# Revit family: Casement_38_I_Top_Hung_Standard
name_source: partatom
category: Windows
revit_build: Autodesk Revit 2014 (Build: 20130308_1515(x64)
units: mm (PartAtom-declared; Revit-internal decimal feet)

## types (24) — shared parameters
Aluminium Thickness = 1 mm  [stored 0.00328084 ft]
Bead SG Gap = 13 mm  [stored 0.0426509 ft]
Bottom Hung = No
Casement Dimension = 38 mm  [stored 0.124672 ft]
Custom Sash Bottom Height = 554 mm  [stored 1.81759 ft]
Custom Sash Top Height = 554 mm  [stored 1.81759 ft]
DG Extrusion Start = 9 mm  [stored 0.0295276 ft]
DG Gasket Finish = Double Glazing Gasket Material
Default Sill Height = 800 mm  [stored 2.62467 ft]
Depth Bead = 24 mm  [stored 0.0787402 ft]
Description = Window 38mm, Type I top hung
Frame Center Offset = 19 mm  [stored 0.062336 ft]
Height Panel 1 = 540 mm  [stored 1.77165 ft]
Height Panel 2 = 540 mm  [stored 1.77165 ft]
Height Sash Bottom = 524 mm  [stored 1.71916 ft]
Height Sash Bottom Opening = 554 mm  [stored 1.81759 ft]
Height Sash Top = 524 mm  [stored 1.71916 ft]
Height Sash Top Opening = 554 mm  [stored 1.81759 ft]
Limit Fixed Pane Height Max = 1800 mm
Limit Fixed Pane Height Min = 200 mm  [stored 0.656168 ft]
Limit Fixed Pane Width Max = 1500 mm
Limit Fixed Pane Width Min = 200 mm  [stored 0.656168 ft]
Limit Sash Bottom Height Min = 300 mm  [stored 0.984252 ft]
Limit Sash Top Height Max = 1200 mm
Limit Sash Top Height Min = 300 mm  [stored 0.984252 ft]
Limit Sash Width Max = 1500 mm
Limit Sash Width Min = 300 mm  [stored 0.984252 ft]
Limit Window Height Max = 1860 mm
Limit Window Height Min = 1400 mm
Manufacturer = Crealco
Max System DG One Piece Thickness = 6 mm  [stored 0.019685 ft]
Max System DG Unit Thickness = 25 mm  [stored 0.082021 ft]
Model = Casement 38
Offset Bead SG Center Reversed = 19 mm  [stored 0.062336 ft]
Offset Panel 3 Bead Top = 1170 mm
Offset Sash 1 Top = 23 mm  [stored 0.0754593 ft]
Offset Sash 2 Top = 593 mm  [stored 1.94554 ft]
Offset Sash Left = 23 mm  [stored 0.0754593 ft]
Offset Transom 1 Top = 570 mm  [stored 1.87008 ft]
Offset Transom 2 Top = 1140 mm
Offset Window Exterior = 19 mm  [stored 0.062336 ft]
SG Gasket Thickness = 6 mm  [stored 0.019685 ft]
Sash Center Offset = 16 mm  [stored 0.0524934 ft]
Sash Overlap = 7 mm  [stored 0.0229659 ft]
Sash Spacing Inner = 8 mm  [stored 0.0262467 ft]
Top Hung = Yes
URL = http://www.crealco.co.za
Wall Closure = By host
Width Bead = 15 mm  [stored 0.0492126 ft]
Width Profile = 30 mm  [stored 0.0984252 ft]
zero-valued in all types: Window Exterior Offset

## per-type parameters (varying)
- 38-1215DT-1000Pa: Area Pane Left Bottom=0.15 m²; Area Pane Left Middle=0.23 m²; Area Pane Left Top=0.23 m²; Area Pane Right=0.78 m²; Clearvue Insulated LowE SHGC Value=0.709; Clearvue Insulated LowE U Value=5; Clearvue Insulated SHGC Value=0.778; Clearvue Insulated U Value=5.75; Clearvue SHGC Value=0.987; Clearvue U Value=8.9; Custom Sash Width=554 mm  [stored 1.81759 ft]; Custom Windload=1000 mm; Custom Window Height=1490 mm; Custom Window Width=1190 mm; DG Thickness Calc=4 mm  [stored 0.0131234 ft]; Depth Mullion=39 mm  [stored 0.127953 ft]; Energy Advantage SHGC Value=0.804; Energy Advantage U Value=6.7; Height=1490 mm; Height Panel 3=290 mm  [stored 0.951444 ft]; Height Panel 4=1430 mm; Intruderprufe Insulated LowE SHGC Value=0.658; Intruderprufe Insulated LowE U Value=4.9; Intruderprufe Insulated SHGC Value=0.722; Intruderprufe Insulated U Value=5.61; Intruderprufe LowE SHGC Value=0.747; Intruderprufe LowE U Value=6.54; Intruderprufe SHGC Value=0.872; Intruderprufe U Value=8.8; Length Mullion=1490 mm; Length Transom=540 mm  [stored 1.77165 ft]; Limit Sash Bottom Height Max=644 mm  [stored 2.11286 ft]; Limit Sash Bottom Height Max Based On Top Sash=644 mm  [stored 2.11286 ft]; Limit Sash Bottom Height Max Calc=644 mm  [stored 2.11286 ft]; Limit Window Width Max=2130 mm; Limit Window Width Min=830 mm  [stored 2.7231 ft]; Max Pane Area=0.78 m²; Mullion Depth Windload Based=39 mm  [stored 0.127953 ft]; Offset Mullion Left=570 mm  [stored 1.87008 ft]; Offset Panel 4 Left=600 mm  [stored 1.9685 ft]; Width=1190 mm; Width Panel 1=540 mm  [stored 1.77165 ft]; Width Panel 2=540 mm  [stored 1.77165 ft]; Width Panel 3=540 mm  [stored 1.77165 ft]; Width Panel 4=560 mm  [stored 1.83727 ft]; Width Sash 1=524 mm  [stored 1.71916 ft]; Width Sash 2=524 mm  [stored 1.71916 ft]; Width Sash Opening=554 mm  [stored 1.81759 ft]; Windload Design=1000 mm
- 38-1215DT-1500Pa: Area Pane Left Bottom=0.15 m²; Area Pane Left Middle=0.23 m²; Area Pane Left Top=0.23 m²; Area Pane Right=0.78 m²; Clearvue Insulated LowE SHGC Value=0.709; Clearvue Insulated LowE U Value=5.06; Clearvue Insulated SHGC Value=0.779; Clearvue Insulated U Value=5.81; Clearvue SHGC Value=0.896; Clearvue U Value=8.9; Custom Sash Width=554 mm  [stored 1.81759 ft]; Custom Windload=1500 mm; Custom Window Height=1490 mm; Custom Window Width=1190 mm; DG Thickness Calc=4 mm  [stored 0.0131234 ft]; Depth Mullion=54 mm  [stored 0.177165 ft]; Energy Advantage SHGC Value=0.803; Energy Advantage U Value=6.77; Height=1490 mm; Height Panel 3=290 mm  [stored 0.951444 ft]; Height Panel 4=1430 mm; Intruderprufe Insulated LowE SHGC Value=0.66; Intruderprufe Insulated LowE U Value=4.95; Intruderprufe Insulated SHGC Value=0.724; Intruderprufe Insulated U Value=5.67; Intruderprufe LowE SHGC Value=0.749; Intruderprufe LowE U Value=6.61; Intruderprufe SHGC Value=0.859; Intruderprufe U Value=8.82; Length Mullion=1490 mm; Length Transom=540 mm  [stored 1.77165 ft]; Limit Sash Bottom Height Max=644 mm  [stored 2.11286 ft]; Limit Sash Bottom Height Max Based On Top Sash=644 mm  [stored 2.11286 ft]; Limit Sash Bottom Height Max Calc=644 mm  [stored 2.11286 ft]; Limit Window Width Max=2130 mm; Limit Window Width Min=830 mm  [stored 2.7231 ft]; Max Pane Area=0.78 m²; Mullion Depth Windload Based=54 mm  [stored 0.177165 ft]; Offset Mullion Left=570 mm  [stored 1.87008 ft]; Offset Panel 4 Left=600 mm  [stored 1.9685 ft]; Width=1190 mm; Width Panel 1=540 mm  [stored 1.77165 ft]; Width Panel 2=540 mm  [stored 1.77165 ft]; Width Panel 3=540 mm  [stored 1.77165 ft]; Width Panel 4=560 mm  [stored 1.83727 ft]; Width Sash 1=524 mm  [stored 1.71916 ft]; Width Sash 2=524 mm  [stored 1.71916 ft]; Width Sash Opening=554 mm  [stored 1.81759 ft]; Windload Design=1500 mm
- 38-1215DT-2000Pa: Area Pane Left Bottom=0.15 m²; Area Pane Left Middle=0.23 m²; Area Pane Left Top=0.23 m²; Area Pane Right=0.78 m²; Clearvue Insulated LowE SHGC Value=0.709; Clearvue Insulated LowE U Value=5.06; Clearvue Insulated SHGC Value=0.779; Clearvue Insulated U Value=5.81; Clearvue SHGC Value=0.896; Clearvue U Value=8.9; Custom Sash Width=554 mm  [stored 1.81759 ft]; Custom Windload=2000 mm; Custom Window Height=1490 mm; Custom Window Width=1190 mm; DG Thickness Calc=4 mm  [stored 0.0131234 ft]; Depth Mullion=54 mm  [stored 0.177165 ft]; Energy Advantage SHGC Value=0.803; Energy Advantage U Value=6.77; Height=1490 mm; Height Panel 3=290 mm  [stored 0.951444 ft]; Height Panel 4=1430 mm; Intruderprufe Insulated LowE SHGC Value=0.66; Intruderprufe Insulated LowE U Value=4.95; Intruderprufe Insulated SHGC Value=0.724; Intruderprufe Insulated U Value=5.67; Intruderprufe LowE SHGC Value=0.749; Intruderprufe LowE U Value=6.61; Intruderprufe SHGC Value=0.859; Intruderprufe U Value=8.82; Length Mullion=1490 mm; Length Transom=540 mm  [stored 1.77165 ft]; Limit Sash Bottom Height Max=644 mm  [stored 2.11286 ft]; Limit Sash Bottom Height Max Based On Top Sash=644 mm  [stored 2.11286 ft]; Limit Sash Bottom Height Max Calc=644 mm  [stored 2.11286 ft]; Limit Window Width Max=2130 mm; Limit Window Width Min=830 mm  [stored 2.7231 ft]; Max Pane Area=0.78 m²; Mullion Depth Windload Based=54 mm  [stored 0.177165 ft]; Offset Mullion Left=570 mm  [stored 1.87008 ft]; Offset Panel 4 Left=600 mm  [stored 1.9685 ft]; Width=1190 mm; Width Panel 1=540 mm  [stored 1.77165 ft]; Width Panel 2=540 mm  [stored 1.77165 ft]; Width Panel 3=540 mm  [stored 1.77165 ft]; Width Panel 4=560 mm  [stored 1.83727 ft]; Width Sash 1=524 mm  [stored 1.71916 ft]; Width Sash 2=524 mm  [stored 1.71916 ft]; Width Sash Opening=554 mm  [stored 1.81759 ft]; Windload Design=2000 mm
- 38-1515DT-1000Pa: Area Pane Left Bottom=0.15 m²; Area Pane Left Middle=0.23 m²; Area Pane Left Top=0.23 m²; Area Pane Right=1.21 m²; Clearvue Insulated LowE SHGC Value=0.822; Clearvue Insulated LowE U Value=5.14; Clearvue Insulated SHGC Value=0.904; Clearvue Insulated U Value=6.03; Clearvue SHGC Value=1.037; Clearvue U Value=9.66; Custom Sash Width=554 mm  [stored 1.81759 ft]; Custom Windload=1000 mm; Custom Window Height=1490 mm; Custom Window Width=1490 mm; DG Thickness Calc=4 mm  [stored 0.0131234 ft]; Depth Mullion=54 mm  [stored 0.177165 ft]; Energy Advantage SHGC Value=0.928; Energy Advantage U Value=7.19; Height=1490 mm; Height Panel 3=290 mm  [stored 0.951444 ft]; Height Panel 4=1430 mm; Intruderprufe Insulated LowE SHGC Value=0.763; Intruderprufe Insulated LowE U Value=5.04; Intruderprufe Insulated SHGC Value=0.839; Intruderprufe Insulated U Value=5.89; Intruderprufe LowE SHGC Value=0.865; Intruderprufe LowE U Value=6.99; Intruderprufe SHGC Value=0.989; Intruderprufe U Value=9.55; Length Mullion=1490 mm; Length Transom=540 mm  [stored 1.77165 ft]; Limit Sash Bottom Height Max=644 mm  [stored 2.11286 ft]; Limit Sash Bottom Height Max Based On Top Sash=644 mm  [stored 2.11286 ft]; Limit Sash Bottom Height Max Calc=644 mm  [stored 2.11286 ft]; Limit Window Width Max=2130 mm; Limit Window Width Min=830 mm  [stored 2.7231 ft]; Max Pane Area=1.21 m²; Mullion Depth Windload Based=54 mm  [stored 0.177165 ft]; Offset Mullion Left=570 mm  [stored 1.87008 ft]; Offset Panel 4 Left=600 mm  [stored 1.9685 ft]; Width=1490 mm; Width Panel 1=540 mm  [stored 1.77165 ft]; Width Panel 2=540 mm  [stored 1.77165 ft]; Width Panel 3=540 mm  [stored 1.77165 ft]; Width Panel 4=860 mm  [stored 2.82152 ft]; Width Sash 1=524 mm  [stored 1.71916 ft]; Width Sash 2=524 mm  [stored 1.71916 ft]; Width Sash Opening=554 mm  [stored 1.81759 ft]; Windload Design=1000 mm
- 38-1515DT-1500Pa: Area Pane Left Bottom=0.15 m²; Area Pane Left Middle=0.23 m²; Area Pane Left Top=0.23 m²; Area Pane Right=1.21 m²; Clearvue Insulated LowE SHGC Value=0.822; Clearvue Insulated LowE U Value=5.14; Clearvue Insulated SHGC Value=0.904; Clearvue Insulated U Value=6.03; Clearvue SHGC Value=1.037; Clearvue U Value=9.66; Custom Sash Width=554 mm  [stored 1.81759 ft]; Custom Windload=1500 mm; Custom Window Height=1490 mm; Custom Window Width=1490 mm; DG Thickness Calc=4 mm  [stored 0.0131234 ft]; Depth Mullion=54 mm  [stored 0.177165 ft]; Energy Advantage SHGC Value=0.928; Energy Advantage U Value=7.19; Height=1490 mm; Height Panel 3=290 mm  [stored 0.951444 ft]; Height Panel 4=1430 mm; Intruderprufe Insulated LowE SHGC Value=0.763; Intruderprufe Insulated LowE U Value=5.04; Intruderprufe Insulated SHGC Value=0.839; Intruderprufe Insulated U Value=5.89; Intruderprufe LowE SHGC Value=0.865; Intruderprufe LowE U Value=6.99; Intruderprufe SHGC Value=0.989; Intruderprufe U Value=9.55; Length Mullion=1490 mm; Length Transom=540 mm  [stored 1.77165 ft]; Limit Sash Bottom Height Max=644 mm  [stored 2.11286 ft]; Limit Sash Bottom Height Max Based On Top Sash=644 mm  [stored 2.11286 ft]; Limit Sash Bottom Height Max Calc=644 mm  [stored 2.11286 ft]; Limit Window Width Max=2130 mm; Limit Window Width Min=830 mm  [stored 2.7231 ft]; Max Pane Area=1.21 m²; Mullion Depth Windload Based=54 mm  [stored 0.177165 ft]; Offset Mullion Left=570 mm  [stored 1.87008 ft]; Offset Panel 4 Left=600 mm  [stored 1.9685 ft]; Width=1490 mm; Width Panel 1=540 mm  [stored 1.77165 ft]; Width Panel 2=540 mm  [stored 1.77165 ft]; Width Panel 3=540 mm  [stored 1.77165 ft]; Width Panel 4=860 mm  [stored 2.82152 ft]; Width Sash 1=524 mm  [stored 1.71916 ft]; Width Sash 2=524 mm  [stored 1.71916 ft]; Width Sash Opening=554 mm  [stored 1.81759 ft]; Windload Design=1500 mm
- 38-1515DT-2000Pa: Area Pane Left Bottom=0.15 m²; Area Pane Left Middle=0.23 m²; Area Pane Left Top=0.23 m²; Area Pane Right=1.21 m²; Clearvue Insulated LowE SHGC Value=0.822; Clearvue Insulated LowE U Value=5.14; Clearvue Insulated SHGC Value=0.904; Clearvue Insulated U Value=6.03; Clearvue SHGC Value=1.037; Clearvue U Value=9.66; Custom Sash Width=554 mm  [stored 1.81759 ft]; Custom Windload=2000 mm; Custom Window Height=1490 mm; Custom Window Width=1490 mm; DG Thickness Calc=4 mm  [stored 0.0131234 ft]; Depth Mullion=54 mm  [stored 0.177165 ft]; Energy Advantage SHGC Value=0.928; Energy Advantage U Value=7.19; Height=1490 mm; Height Panel 3=290 mm  [stored 0.951444 ft]; Height Panel 4=1430 mm; Intruderprufe Insulated LowE SHGC Value=0.763; Intruderprufe Insulated LowE U Value=5.04; Intruderprufe Insulated SHGC Value=0.839; Intruderprufe Insulated U Value=5.89; Intruderprufe LowE SHGC Value=0.865; Intruderprufe LowE U Value=6.99; Intruderprufe SHGC Value=0.989; Intruderprufe U Value=9.55; Length Mullion=1490 mm; Length Transom=540 mm  [stored 1.77165 ft]; Limit Sash Bottom Height Max=644 mm  [stored 2.11286 ft]; Limit Sash Bottom Height Max Based On Top Sash=644 mm  [stored 2.11286 ft]; Limit Sash Bottom Height Max Calc=644 mm  [stored 2.11286 ft]; Limit Window Width Max=2130 mm; Limit Window Width Min=830 mm  [stored 2.7231 ft]; Max Pane Area=1.21 m²; Mullion Depth Windload Based=54 mm  [stored 0.177165 ft]; Offset Mullion Left=570 mm  [stored 1.87008 ft]; Offset Panel 4 Left=600 mm  [stored 1.9685 ft]; Width=1490 mm; Width Panel 1=540 mm  [stored 1.77165 ft]; Width Panel 2=540 mm  [stored 1.77165 ft]; Width Panel 3=540 mm  [stored 1.77165 ft]; Width Panel 4=860 mm  [stored 2.82152 ft]; Width Sash 1=524 mm  [stored 1.71916 ft]; Width Sash 2=524 mm  [stored 1.71916 ft]; Width Sash Opening=554 mm  [stored 1.81759 ft]; Windload Design=2000 mm
- 38-1815DT-1000Pa: Area Pane Left Bottom=0.23 m²; Area Pane Left Middle=0.38 m²; Area Pane Left Top=0.38 m²; Area Pane Right=1.21 m²; Clearvue Insulated LowE SHGC Value=0.755; Clearvue Insulated LowE U Value=4.65; Clearvue Insulated SHGC Value=0.83; Clearvue Insulated U Value=5.47; Clearvue SHGC Value=0.955; Clearvue U Value=8.8; Custom Sash Width=854 mm  [stored 2.80184 ft]; Custom Windload=1000 mm; Custom Window Height=1490 mm; Custom Window Width=1790 mm; DG Thickness Calc=4 mm  [stored 0.0131234 ft]; Depth Mullion=54 mm  [stored 0.177165 ft]; Energy Advantage SHGC Value=0.854; Energy Advantage U Value=6.5; Height=1490 mm; Height Panel 3=290 mm  [stored 0.951444 ft]; Height Panel 4=1430 mm; Intruderprufe Insulated LowE SHGC Value=0.7; Intruderprufe Insulated LowE U Value=4.56; Intruderprufe Insulated SHGC Value=0.77; Intruderprufe Insulated U Value=5.34; Intruderprufe LowE SHGC Value=0.794; Intruderprufe LowE U Value=6.35; Intruderprufe SHGC Value=0.914; Intruderprufe U Value=8.73; Length Mullion=1490 mm; Length Transom=840 mm; Limit Sash Bottom Height Max=644 mm  [stored 2.11286 ft]; Limit Sash Bottom Height Max Based On Top Sash=644 mm  [stored 2.11286 ft]; Limit Sash Bottom Height Max Calc=644 mm  [stored 2.11286 ft]; Limit Window Width Max=2430 mm; Limit Window Width Min=1130 mm; Max Pane Area=1.21 m²; Mullion Depth Windload Based=54 mm  [stored 0.177165 ft]; Offset Mullion Left=870 mm  [stored 2.85433 ft]; Offset Panel 4 Left=900 mm  [stored 2.95276 ft]; Width=1790 mm; Width Panel 1=840 mm; Width Panel 2=840 mm; Width Panel 3=840 mm; Width Panel 4=860 mm  [stored 2.82152 ft]; Width Sash 1=824 mm; Width Sash 2=824 mm; Width Sash Opening=854 mm  [stored 2.80184 ft]; Windload Design=1000 mm
- 38-1815DT-1500Pa: Area Pane Left Bottom=0.23 m²; Area Pane Left Middle=0.38 m²; Area Pane Left Top=0.38 m²; Area Pane Right=1.21 m²; Clearvue Insulated LowE SHGC Value=0.755; Clearvue Insulated LowE U Value=4.65; Clearvue Insulated SHGC Value=0.83; Clearvue Insulated U Value=5.47; Clearvue SHGC Value=0.955; Clearvue U Value=8.8; Custom Sash Width=854 mm  [stored 2.80184 ft]; Custom Windload=1500 mm; Custom Window Height=1490 mm; Custom Window Width=1790 mm; DG Thickness Calc=4 mm  [stored 0.0131234 ft]; Depth Mullion=54 mm  [stored 0.177165 ft]; Energy Advantage SHGC Value=0.854; Energy Advantage U Value=6.5; Height=1490 mm; Height Panel 3=290 mm  [stored 0.951444 ft]; Height Panel 4=1430 mm; Intruderprufe Insulated LowE SHGC Value=0.7; Intruderprufe Insulated LowE U Value=4.56; Intruderprufe Insulated SHGC Value=0.77; Intruderprufe Insulated U Value=5.34; Intruderprufe LowE SHGC Value=0.794; Intruderprufe LowE U Value=6.35; Intruderprufe SHGC Value=0.914; Intruderprufe U Value=8.73; Length Mullion=1490 mm; Length Transom=840 mm; Limit Sash Bottom Height Max=644 mm  [stored 2.11286 ft]; Limit Sash Bottom Height Max Based On Top Sash=644 mm  [stored 2.11286 ft]; Limit Sash Bottom Height Max Calc=644 mm  [stored 2.11286 ft]; Limit Window Width Max=2430 mm; Limit Window Width Min=1130 mm; Max Pane Area=1.21 m²; Mullion Depth Windload Based=54 mm  [stored 0.177165 ft]; Offset Mullion Left=870 mm  [stored 2.85433 ft]; Offset Panel 4 Left=900 mm  [stored 2.95276 ft]; Width=1790 mm; Width Panel 1=840 mm; Width Panel 2=840 mm; Width Panel 3=840 mm; Width Panel 4=860 mm  [stored 2.82152 ft]; Width Sash 1=824 mm; Width Sash 2=824 mm; Width Sash Opening=854 mm  [stored 2.80184 ft]; Windload Design=1500 mm
- 38-1815DT-2000Pa: Area Pane Left Bottom=0.23 m²; Area Pane Left Middle=0.38 m²; Area Pane Left Top=0.38 m²; Area Pane Right=1.21 m²; Clearvue Insulated LowE SHGC Value=0.756; Clearvue Insulated LowE U Value=4.72; Clearvue Insulated SHGC Value=0.831; Clearvue Insulated U Value=5.53; Clearvue SHGC Value=0.955; Clearvue U Value=8.75; Custom Sash Width=854 mm  [stored 2.80184 ft]; Custom Windload=2000 mm; Custom Window Height=1490 mm; Custom Window Width=1790 mm; DG Thickness Calc=4 mm  [stored 0.0131234 ft]; Depth Mullion=70 mm  [stored 0.229659 ft]; Energy Advantage SHGC Value=0.856; Energy Advantage U Value=6.58; Height=1490 mm; Height Panel 3=290 mm  [stored 0.951444 ft]; Height Panel 4=1430 mm; Intruderprufe Insulated LowE SHGC Value=0.7; Intruderprufe Insulated LowE U Value=4.62; Intruderprufe Insulated SHGC Value=0.77; Intruderprufe Insulated U Value=5.4; Intruderprufe LowE SHGC Value=0.794; Intruderprufe LowE U Value=6.43; Intruderprufe SHGC Value=0.906; Intruderprufe U Value=8.74; Length Mullion=1490 mm; Length Transom=840 mm; Limit Sash Bottom Height Max=644 mm  [stored 2.11286 ft]; Limit Sash Bottom Height Max Based On Top Sash=644 mm  [stored 2.11286 ft]; Limit Sash Bottom Height Max Calc=644 mm  [stored 2.11286 ft]; Limit Window Width Max=2430 mm; Limit Window Width Min=1130 mm; Max Pane Area=1.21 m²; Mullion Depth Windload Based=70 mm  [stored 0.229659 ft]; Offset Mullion Left=870 mm  [stored 2.85433 ft]; Offset Panel 4 Left=900 mm  [stored 2.95276 ft]; Width=1790 mm; Width Panel 1=840 mm; Width Panel 2=840 mm; Width Panel 3=840 mm; Width Panel 4=860 mm  [stored 2.82152 ft]; Width Sash 1=824 mm; Width Sash 2=824 mm; Width Sash Opening=854 mm  [stored 2.80184 ft]; Windload Design=2000 mm
- 38-2415DT-1000Pa: Area Pane Left Bottom=0.23 m²; Area Pane Left Middle=0.38 m²; Area Pane Left Top=0.38 m²; Area Pane Right=2.06 m²; Clearvue Insulated LowE SHGC Value=0.892; Clearvue Insulated LowE U Value=4.82; Clearvue Insulated SHGC Value=0.981; Clearvue Insulated U Value=5.81; Clearvue SHGC Value=0; Clearvue U Value=7.9; Custom Sash Width=854 mm  [stored 2.80184 ft]; Custom Windload=1000 mm; Custom Window Height=1490 mm; Custom Window Width=2390 mm; DG Thickness Calc=4 mm  [stored 0.0131234 ft]; Depth Mullion=54 mm  [stored 0.177165 ft]; Energy Advantage SHGC Value=0; Energy Advantage U Value=7.9; Height=1490 mm; Height Panel 3=290 mm  [stored 0.951444 ft]; Height Panel 4=1430 mm; Intruderprufe Insulated LowE SHGC Value=0.825; Intruderprufe Insulated LowE U Value=4.73; Intruderprufe Insulated SHGC Value=0.909; Intruderprufe Insulated U Value=5.68; Intruderprufe LowE SHGC Value=0.936; Intruderprufe LowE U Value=6.88; Intruderprufe SHGC Value=1.072; Intruderprufe U Value=9.68; Length Mullion=1490 mm; Length Transom=840 mm; Limit Sash Bottom Height Max=644 mm  [stored 2.11286 ft]; Limit Sash Bottom Height Max Based On Top Sash=644 mm  [stored 2.11286 ft]; Limit Sash Bottom Height Max Calc=644 mm  [stored 2.11286 ft]; Limit Window Width Max=2430 mm; Limit Window Width Min=1130 mm; Max Pane Area=2.06 m²; Mullion Depth Windload Based=54 mm  [stored 0.177165 ft]; Offset Mullion Left=870 mm  [stored 2.85433 ft]; Offset Panel 4 Left=900 mm  [stored 2.95276 ft]; Width=2390 mm; Width Panel 1=840 mm; Width Panel 2=840 mm; Width Panel 3=840 mm; Width Panel 4=1460 mm; Width Sash 1=824 mm; Width Sash 2=824 mm; Width Sash Opening=854 mm  [stored 2.80184 ft]; Windload Design=1000 mm
- 38-2415DT-1500Pa: Area Pane Left Bottom=0.23 m²; Area Pane Left Middle=0.38 m²; Area Pane Left Top=0.38 m²; Area Pane Right=2.06 m²; Clearvue Insulated LowE SHGC Value=0.893; Clearvue Insulated LowE U Value=4.88; Clearvue Insulated SHGC Value=0.982; Clearvue Insulated U Value=5.86; Clearvue SHGC Value=0; Clearvue U Value=7.9; Custom Sash Width=854 mm  [stored 2.80184 ft]; Custom Windload=1500 mm; Custom Window Height=1490 mm; Custom Window Width=2390 mm; DG Thickness Calc=4 mm  [stored 0.0131234 ft]; Depth Mullion=54 mm  [stored 0.177165 ft]; Energy Advantage SHGC Value=0; Energy Advantage U Value=7.9; Height=1490 mm; Height Panel 3=290 mm  [stored 0.951444 ft]; Height Panel 4=1430 mm; Intruderprufe Insulated LowE SHGC Value=0.825; Intruderprufe Insulated LowE U Value=4.78; Intruderprufe Insulated SHGC Value=0.91; Intruderprufe Insulated U Value=5.73; Intruderprufe LowE SHGC Value=0.936; Intruderprufe LowE U Value=6.95; Intruderprufe SHGC Value=1.065; Intruderprufe U Value=9.69; Length Mullion=1490 mm; Length Transom=840 mm; Limit Sash Bottom Height Max=644 mm  [stored 2.11286 ft]; Limit Sash Bottom Height Max Based On Top Sash=644 mm  [stored 2.11286 ft]; Limit Sash Bottom Height Max Calc=644 mm  [stored 2.11286 ft]; Limit Window Width Max=2430 mm; Limit Window Width Min=1130 mm; Max Pane Area=2.06 m²; Mullion Depth Windload Based=54 mm  [stored 0.177165 ft]; Offset Mullion Left=870 mm  [stored 2.85433 ft]; Offset Panel 4 Left=900 mm  [stored 2.95276 ft]; Width=2390 mm; Width Panel 1=840 mm; Width Panel 2=840 mm; Width Panel 3=840 mm; Width Panel 4=1460 mm; Width Sash 1=824 mm; Width Sash 2=824 mm; Width Sash Opening=854 mm  [stored 2.80184 ft]; Windload Design=1500 mm
- 38-2415DT-2000Pa: Area Pane Left Bottom=0.23 m²; Area Pane Left Middle=0.38 m²; Area Pane Left Top=0.38 m²; Area Pane Right=2.06 m²; Clearvue Insulated LowE SHGC Value=0.893; Clearvue Insulated LowE U Value=4.88; Clearvue Insulated SHGC Value=0.982; Clearvue Insulated U Value=5.86; Clearvue SHGC Value=0; Clearvue U Value=7.9; Custom Sash Width=854 mm  [stored 2.80184 ft]; Custom Windload=2000 mm; Custom Window Height=1490 mm; Custom Window Width=2390 mm; DG Thickness Calc=4 mm  [stored 0.0131234 ft]; Depth Mullion=70 mm  [stored 0.229659 ft]; Energy Advantage SHGC Value=0; Energy Advantage U Value=7.9; Height=1490 mm; Height Panel 3=290 mm  [stored 0.951444 ft]; Height Panel 4=1430 mm; Intruderprufe Insulated LowE SHGC Value=0.825; Intruderprufe Insulated LowE U Value=4.78; Intruderprufe Insulated SHGC Value=0.91; Intruderprufe Insulated U Value=5.73; Intruderprufe LowE SHGC Value=0.936; Intruderprufe LowE U Value=6.95; Intruderprufe SHGC Value=1.065; Intruderprufe U Value=9.69; Length Mullion=1490 mm; Length Transom=840 mm; Limit Sash Bottom Height Max=644 mm  [stored 2.11286 ft]; Limit Sash Bottom Height Max Based On Top Sash=644 mm  [stored 2.11286 ft]; Limit Sash Bottom Height Max Calc=644 mm  [stored 2.11286 ft]; Limit Window Width Max=2430 mm; Limit Window Width Min=1130 mm; Max Pane Area=2.06 m²; Mullion Depth Windload Based=70 mm  [stored 0.229659 ft]; Offset Mullion Left=870 mm  [stored 2.85433 ft]; Offset Panel 4 Left=900 mm  [stored 2.95276 ft]; Width=2390 mm; Width Panel 1=840 mm; Width Panel 2=840 mm; Width Panel 3=840 mm; Width Panel 4=1460 mm; Width Sash 1=824 mm; Width Sash 2=824 mm; Width Sash Opening=854 mm  [stored 2.80184 ft]; Windload Design=2000 mm
- 38-1218DT-1000Pa: Area Pane Left Bottom=0.31 m²; Area Pane Left Middle=0.23 m²; Area Pane Left Top=0.23 m²; Area Pane Right=0.95 m²; Clearvue Insulated LowE SHGC Value=0.767; Clearvue Insulated LowE U Value=5.14; Clearvue Insulated SHGC Value=0.842; Clearvue Insulated U Value=5.95; Clearvue SHGC Value=0.967; Clearvue U Value=9.31; Custom Sash Width=554 mm  [stored 1.81759 ft]; Custom Windload=1000 mm; Custom Window Height=1790 mm; Custom Window Width=1190 mm; DG Thickness Calc=4 mm  [stored 0.0131234 ft]; Depth Mullion=54 mm  [stored 0.177165 ft]; Energy Advantage SHGC Value=0.899; Energy Advantage U Value=6.99; Height=1790 mm; Height Panel 3=590 mm; Height Panel 4=1730 mm; Intruderprufe Insulated LowE SHGC Value=0.712; Intruderprufe Insulated LowE U Value=5.03; Intruderprufe Insulated SHGC Value=0.783; Intruderprufe Insulated U Value=5.81; Intruderprufe LowE SHGC Value=0.808; Intruderprufe LowE U Value=6.84; Intruderprufe SHGC Value=0.924; Intruderprufe U Value=9.21; Length Mullion=1790 mm; Length Transom=540 mm  [stored 1.77165 ft]; Limit Sash Bottom Height Max=944 mm; Limit Sash Bottom Height Max Based On Top Sash=944 mm; Limit Sash Bottom Height Max Calc=944 mm; Limit Window Width Max=2130 mm; Limit Window Width Min=830 mm  [stored 2.7231 ft]; Max Pane Area=0.95 m²; Mullion Depth Windload Based=54 mm  [stored 0.177165 ft]; Offset Mullion Left=570 mm  [stored 1.87008 ft]; Offset Panel 4 Left=600 mm  [stored 1.9685 ft]; Width=1190 mm; Width Panel 1=540 mm  [stored 1.77165 ft]; Width Panel 2=540 mm  [stored 1.77165 ft]; Width Panel 3=540 mm  [stored 1.77165 ft]; Width Panel 4=560 mm  [stored 1.83727 ft]; Width Sash 1=524 mm  [stored 1.71916 ft]; Width Sash 2=524 mm  [stored 1.71916 ft]; Width Sash Opening=554 mm  [stored 1.81759 ft]; Windload Design=1000 mm
- 38-1218DT-1500Pa: Area Pane Left Bottom=0.31 m²; Area Pane Left Middle=0.23 m²; Area Pane Left Top=0.23 m²; Area Pane Right=0.95 m²; Clearvue Insulated LowE SHGC Value=0.768; Clearvue Insulated LowE U Value=5.24; Clearvue Insulated SHGC Value=0.844; Clearvue Insulated U Value=6.05; Clearvue SHGC Value=0.967; Clearvue U Value=9.22; Custom Sash Width=554 mm  [stored 1.81759 ft]; Custom Windload=1500 mm; Custom Window Height=1790 mm; Custom Window Width=1190 mm; DG Thickness Calc=4 mm  [stored 0.0131234 ft]; Depth Mullion=70 mm  [stored 0.229659 ft]; Energy Advantage SHGC Value=0.868; Energy Advantage U Value=7.12; Height=1790 mm; Height Panel 3=590 mm; Height Panel 4=1730 mm; Intruderprufe Insulated LowE SHGC Value=0.713; Intruderprufe Insulated LowE U Value=5.13; Intruderprufe Insulated SHGC Value=0.783; Intruderprufe Insulated U Value=5.9; Intruderprufe LowE SHGC Value=0.808; Intruderprufe LowE U Value=6.96; Intruderprufe SHGC Value=0.911; Intruderprufe U Value=9.23; Length Mullion=1790 mm; Length Transom=540 mm  [stored 1.77165 ft]; Limit Sash Bottom Height Max=944 mm; Limit Sash Bottom Height Max Based On Top Sash=944 mm; Limit Sash Bottom Height Max Calc=944 mm; Limit Window Width Max=2130 mm; Limit Window Width Min=830 mm  [stored 2.7231 ft]; Max Pane Area=0.95 m²; Mullion Depth Windload Based=70 mm  [stored 0.229659 ft]; Offset Mullion Left=570 mm  [stored 1.87008 ft]; Offset Panel 4 Left=600 mm  [stored 1.9685 ft]; Width=1190 mm; Width Panel 1=540 mm  [stored 1.77165 ft]; Width Panel 2=540 mm  [stored 1.77165 ft]; Width Panel 3=540 mm  [stored 1.77165 ft]; Width Panel 4=560 mm  [stored 1.83727 ft]; Width Sash 1=524 mm  [stored 1.71916 ft]; Width Sash 2=524 mm  [stored 1.71916 ft]; Width Sash Opening=554 mm  [stored 1.81759 ft]; Windload Design=1500 mm
- 38-1218DT-2000Pa: Area Pane Left Bottom=0.31 m²; Area Pane Left Middle=0.23 m²; Area Pane Left Top=0.23 m²; Area Pane Right=0.95 m²; Clearvue Insulated LowE SHGC Value=0.768; Clearvue Insulated LowE U Value=5.24; Clearvue Insulated SHGC Value=0.844; Clearvue Insulated U Value=6.05; Clearvue SHGC Value=0.967; Clearvue U Value=9.22; Custom Sash Width=554 mm  [stored 1.81759 ft]; Custom Windload=2000 mm; Custom Window Height=1790 mm; Custom Window Width=1190 mm; DG Thickness Calc=4 mm  [stored 0.0131234 ft]; Depth Mullion=70 mm  [stored 0.229659 ft]; Energy Advantage SHGC Value=0.868; Energy Advantage U Value=7.12; Height=1790 mm; Height Panel 3=590 mm; Height Panel 4=1730 mm; Intruderprufe Insulated LowE SHGC Value=0.713; Intruderprufe Insulated LowE U Value=5.13; Intruderprufe Insulated SHGC Value=0.783; Intruderprufe Insulated U Value=5.9; Intruderprufe LowE SHGC Value=0.808; Intruderprufe LowE U Value=6.96; Intruderprufe SHGC Value=0.911; Intruderprufe U Value=9.23; Length Mullion=1790 mm; Length Transom=540 mm  [stored 1.77165 ft]; Limit Sash Bottom Height Max=944 mm; Limit Sash Bottom Height Max Based On Top Sash=944 mm; Limit Sash Bottom Height Max Calc=944 mm; Limit Window Width Max=2130 mm; Limit Window Width Min=830 mm  [stored 2.7231 ft]; Max Pane Area=0.95 m²; Mullion Depth Windload Based=70 mm  [stored 0.229659 ft]; Offset Mullion Left=570 mm  [stored 1.87008 ft]; Offset Panel 4 Left=600 mm  [stored 1.9685 ft]; Width=1190 mm; Width Panel 1=540 mm  [stored 1.77165 ft]; Width Panel 2=540 mm  [stored 1.77165 ft]; Width Panel 3=540 mm  [stored 1.77165 ft]; Width Panel 4=560 mm  [stored 1.83727 ft]; Width Sash 1=524 mm  [stored 1.71916 ft]; Width Sash 2=524 mm  [stored 1.71916 ft]; Width Sash Opening=554 mm  [stored 1.81759 ft]; Windload Design=2000 mm
- 38-1518DT-1000Pa: Area Pane Left Bottom=0.31 m²; Area Pane Left Middle=0.23 m²; Area Pane Left Top=0.23 m²; Area Pane Right=1.46 m²; Clearvue Insulated LowE SHGC Value=0.899; Clearvue Insulated LowE U Value=5.31; Clearvue Insulated SHGC Value=0.988; Clearvue Insulated U Value=6.29; Clearvue SHGC Value=0; Clearvue U Value=7.9; Custom Sash Width=554 mm  [stored 1.81759 ft]; Custom Windload=1000 mm; Custom Window Height=1790 mm; Custom Window Width=1490 mm; DG Thickness Calc=4 mm  [stored 0.0131234 ft]; Depth Mullion=54 mm  [stored 0.177165 ft]; Energy Advantage SHGC Value=0; Energy Advantage U Value=7.9; Height=1790 mm; Height Panel 3=590 mm; Height Panel 4=1730 mm; Intruderprufe Insulated LowE SHGC Value=0.833; Intruderprufe Insulated LowE U Value=5.2; Intruderprufe Insulated SHGC Value=0.918; Intruderprufe Insulated U Value=6.14; Intruderprufe LowE SHGC Value=0.945; Intruderprufe LowE U Value=7.36; Intruderprufe SHGC Value=1.078; Intruderprufe U Value=10.15; Length Mullion=1790 mm; Length Transom=540 mm  [stored 1.77165 ft]; Limit Sash Bottom Height Max=944 mm; Limit Sash Bottom Height Max Based On Top Sash=944 mm; Limit Sash Bottom Height Max Calc=944 mm; Limit Window Width Max=2130 mm; Limit Window Width Min=830 mm  [stored 2.7231 ft]; Max Pane Area=1.46 m²; Mullion Depth Windload Based=54 mm  [stored 0.177165 ft]; Offset Mullion Left=570 mm  [stored 1.87008 ft]; Offset Panel 4 Left=600 mm  [stored 1.9685 ft]; Width=1490 mm; Width Panel 1=540 mm  [stored 1.77165 ft]; Width Panel 2=540 mm  [stored 1.77165 ft]; Width Panel 3=540 mm  [stored 1.77165 ft]; Width Panel 4=860 mm  [stored 2.82152 ft]; Width Sash 1=524 mm  [stored 1.71916 ft]; Width Sash 2=524 mm  [stored 1.71916 ft]; Width Sash Opening=554 mm  [stored 1.81759 ft]; Windload Design=1000 mm
- 38-1518DT-1500Pa: Area Pane Left Bottom=0.31 m²; Area Pane Left Middle=0.23 m²; Area Pane Left Top=0.23 m²; Area Pane Right=1.46 m²; Clearvue Insulated LowE SHGC Value=0.901; Clearvue Insulated LowE U Value=5.4; Clearvue Insulated SHGC Value=0.99; Clearvue Insulated U Value=6.38; Clearvue SHGC Value=0; Clearvue U Value=7.9; Custom Sash Width=554 mm  [stored 1.81759 ft]; Custom Windload=1500 mm; Custom Window Height=1790 mm; Custom Window Width=1490 mm; DG Thickness Calc=4 mm  [stored 0.0131234 ft]; Depth Mullion=70 mm  [stored 0.229659 ft]; Energy Advantage SHGC Value=0; Energy Advantage U Value=7.9; Height=1790 mm; Height Panel 3=590 mm; Height Panel 4=1730 mm; Intruderprufe Insulated LowE SHGC Value=0.834; Intruderprufe Insulated LowE U Value=5.29; Intruderprufe Insulated SHGC Value=0.918; Intruderprufe Insulated U Value=6.22; Intruderprufe LowE SHGC Value=0.945; Intruderprufe LowE U Value=7.47; Intruderprufe SHGC Value=1.067; Intruderprufe U Value=10.16; Length Mullion=1790 mm; Length Transom=540 mm  [stored 1.77165 ft]; Limit Sash Bottom Height Max=944 mm; Limit Sash Bottom Height Max Based On Top Sash=944 mm; Limit Sash Bottom Height Max Calc=944 mm; Limit Window Width Max=2130 mm; Limit Window Width Min=830 mm  [stored 2.7231 ft]; Max Pane Area=1.46 m²; Mullion Depth Windload Based=70 mm  [stored 0.229659 ft]; Offset Mullion Left=570 mm  [stored 1.87008 ft]; Offset Panel 4 Left=600 mm  [stored 1.9685 ft]; Width=1490 mm; Width Panel 1=540 mm  [stored 1.77165 ft]; Width Panel 2=540 mm  [stored 1.77165 ft]; Width Panel 3=540 mm  [stored 1.77165 ft]; Width Panel 4=860 mm  [stored 2.82152 ft]; Width Sash 1=524 mm  [stored 1.71916 ft]; Width Sash 2=524 mm  [stored 1.71916 ft]; Width Sash Opening=554 mm  [stored 1.81759 ft]; Windload Design=1500 mm
- 38-1518DT-2000Pa: Area Pane Left Bottom=0.31 m²; Area Pane Left Middle=0.23 m²; Area Pane Left Top=0.23 m²; Area Pane Right=1.46 m²; Clearvue Insulated LowE SHGC Value=0.901; Clearvue Insulated LowE U Value=5.4; Clearvue Insulated SHGC Value=0.99; Clearvue Insulated U Value=6.38; Clearvue SHGC Value=0; Clearvue U Value=7.9; Custom Sash Width=554 mm  [stored 1.81759 ft]; Custom Windload=2000 mm; Custom Window Height=1790 mm; Custom Window Width=1490 mm; DG Thickness Calc=4 mm  [stored 0.0131234 ft]; Depth Mullion=70 mm  [stored 0.229659 ft]; Energy Advantage SHGC Value=0; Energy Advantage U Value=7.9; Height=1790 mm; Height Panel 3=590 mm; Height Panel 4=1730 mm; Intruderprufe Insulated LowE SHGC Value=0.834; Intruderprufe Insulated LowE U Value=5.29; Intruderprufe Insulated SHGC Value=0.918; Intruderprufe Insulated U Value=6.22; Intruderprufe LowE SHGC Value=0.945; Intruderprufe LowE U Value=7.47; Intruderprufe SHGC Value=1.067; Intruderprufe U Value=10.16; Length Mullion=1790 mm; Length Transom=540 mm  [stored 1.77165 ft]; Limit Sash Bottom Height Max=944 mm; Limit Sash Bottom Height Max Based On Top Sash=944 mm; Limit Sash Bottom Height Max Calc=944 mm; Limit Window Width Max=2130 mm; Limit Window Width Min=830 mm  [stored 2.7231 ft]; Max Pane Area=1.46 m²; Mullion Depth Windload Based=70 mm  [stored 0.229659 ft]; Offset Mullion Left=570 mm  [stored 1.87008 ft]; Offset Panel 4 Left=600 mm  [stored 1.9685 ft]; Width=1490 mm; Width Panel 1=540 mm  [stored 1.77165 ft]; Width Panel 2=540 mm  [stored 1.77165 ft]; Width Panel 3=540 mm  [stored 1.77165 ft]; Width Panel 4=860 mm  [stored 2.82152 ft]; Width Sash 1=524 mm  [stored 1.71916 ft]; Width Sash 2=524 mm  [stored 1.71916 ft]; Width Sash Opening=554 mm  [stored 1.81759 ft]; Windload Design=2000 mm
- 38-1818DT-1000Pa: Area Pane Left Bottom=0.48 m²; Area Pane Left Middle=0.38 m²; Area Pane Left Top=0.38 m²; Area Pane Right=1.46 m²; Clearvue Insulated LowE SHGC Value=0.816; Clearvue Insulated LowE U Value=4.77; Clearvue Insulated SHGC Value=0.897; Clearvue Insulated U Value=5.66; Clearvue SHGC Value=0; Clearvue U Value=7.9; Custom Sash Width=854 mm  [stored 2.80184 ft]; Custom Windload=1000 mm; Custom Window Height=1790 mm; Custom Window Width=1790 mm; DG Thickness Calc=4 mm  [stored 0.0131234 ft]; Depth Mullion=70 mm  [stored 0.229659 ft]; Energy Advantage SHGC Value=0; Energy Advantage U Value=7.9; Height=1790 mm; Height Panel 3=590 mm; Height Panel 4=1730 mm; Intruderprufe Insulated LowE SHGC Value=0.755; Intruderprufe Insulated LowE U Value=4.67; Intruderprufe Insulated SHGC Value=0.831; Intruderprufe Insulated U Value=5.53; Intruderprufe LowE SHGC Value=0.856; Intruderprufe LowE U Value=6.64; Intruderprufe SHGC Value=0.974; Intruderprufe U Value=9.12; Length Mullion=1790 mm; Length Transom=840 mm; Limit Sash Bottom Height Max=944 mm; Limit Sash Bottom Height Max Based On Top Sash=944 mm; Limit Sash Bottom Height Max Calc=944 mm; Limit Window Width Max=2430 mm; Limit Window Width Min=1130 mm; Max Pane Area=1.46 m²; Mullion Depth Windload Based=70 mm  [stored 0.229659 ft]; Offset Mullion Left=870 mm  [stored 2.85433 ft]; Offset Panel 4 Left=900 mm  [stored 2.95276 ft]; Width=1790 mm; Width Panel 1=840 mm; Width Panel 2=840 mm; Width Panel 3=840 mm; Width Panel 4=860 mm  [stored 2.82152 ft]; Width Sash 1=824 mm; Width Sash 2=824 mm; Width Sash Opening=854 mm  [stored 2.80184 ft]; Windload Design=1000 mm
- 38-1818DT-1500Pa: Area Pane Left Bottom=0.48 m²; Area Pane Left Middle=0.38 m²; Area Pane Left Top=0.38 m²; Area Pane Right=1.46 m²; Clearvue Insulated LowE SHGC Value=0.816; Clearvue Insulated LowE U Value=4.77; Clearvue Insulated SHGC Value=0.897; Clearvue Insulated U Value=5.66; Clearvue SHGC Value=0; Clearvue U Value=7.9; Custom Sash Width=854 mm  [stored 2.80184 ft]; Custom Windload=1500 mm; Custom Window Height=1790 mm; Custom Window Width=1790 mm; DG Thickness Calc=4 mm  [stored 0.0131234 ft]; Depth Mullion=70 mm  [stored 0.229659 ft]; Energy Advantage SHGC Value=0; Energy Advantage U Value=7.9; Height=1790 mm; Height Panel 3=590 mm; Height Panel 4=1730 mm; Intruderprufe Insulated LowE SHGC Value=0.755; Intruderprufe Insulated LowE U Value=4.67; Intruderprufe Insulated SHGC Value=0.831; Intruderprufe Insulated U Value=5.53; Intruderprufe LowE SHGC Value=0.856; Intruderprufe LowE U Value=6.64; Intruderprufe SHGC Value=0.974; Intruderprufe U Value=9.12; Length Mullion=1790 mm; Length Transom=840 mm; Limit Sash Bottom Height Max=944 mm; Limit Sash Bottom Height Max Based On Top Sash=944 mm; Limit Sash Bottom Height Max Calc=944 mm; Limit Window Width Max=2430 mm; Limit Window Width Min=1130 mm; Max Pane Area=1.46 m²; Mullion Depth Windload Based=70 mm  [stored 0.229659 ft]; Offset Mullion Left=870 mm  [stored 2.85433 ft]; Offset Panel 4 Left=900 mm  [stored 2.95276 ft]; Width=1790 mm; Width Panel 1=840 mm; Width Panel 2=840 mm; Width Panel 3=840 mm; Width Panel 4=860 mm  [stored 2.82152 ft]; Width Sash 1=824 mm; Width Sash 2=824 mm; Width Sash Opening=854 mm  [stored 2.80184 ft]; Windload Design=1500 mm
- 38-1818DT-2000Pa: Area Pane Left Bottom=0.48 m²; Area Pane Left Middle=0.38 m²; Area Pane Left Top=0.38 m²; Area Pane Right=1.46 m²; Clearvue Insulated LowE SHGC Value=0.816; Clearvue Insulated LowE U Value=4.77; Clearvue Insulated SHGC Value=0.897; Clearvue Insulated U Value=5.66; Clearvue SHGC Value=0; Clearvue U Value=7.9; Custom Sash Width=854 mm  [stored 2.80184 ft]; Custom Windload=2000 mm; Custom Window Height=1790 mm; Custom Window Width=1790 mm; DG Thickness Calc=4 mm  [stored 0.0131234 ft]; Depth Mullion=70 mm  [stored 0.229659 ft]; Energy Advantage SHGC Value=0; Energy Advantage U Value=7.9; Height=1790 mm; Height Panel 3=590 mm; Height Panel 4=1730 mm; Intruderprufe Insulated LowE SHGC Value=0.755; Intruderprufe Insulated LowE U Value=4.67; Intruderprufe Insulated SHGC Value=0.831; Intruderprufe Insulated U Value=5.53; Intruderprufe LowE SHGC Value=0.856; Intruderprufe LowE U Value=6.64; Intruderprufe SHGC Value=0.974; Intruderprufe U Value=9.12; Length Mullion=1790 mm; Length Transom=840 mm; Limit Sash Bottom Height Max=944 mm; Limit Sash Bottom Height Max Based On Top Sash=944 mm; Limit Sash Bottom Height Max Calc=944 mm; Limit Window Width Max=2430 mm; Limit Window Width Min=1130 mm; Max Pane Area=1.46 m²; Mullion Depth Windload Based=70 mm  [stored 0.229659 ft]; Offset Mullion Left=870 mm  [stored 2.85433 ft]; Offset Panel 4 Left=900 mm  [stored 2.95276 ft]; Width=1790 mm; Width Panel 1=840 mm; Width Panel 2=840 mm; Width Panel 3=840 mm; Width Panel 4=860 mm  [stored 2.82152 ft]; Width Sash 1=824 mm; Width Sash 2=824 mm; Width Sash Opening=854 mm  [stored 2.80184 ft]; Windload Design=2000 mm
- 38-2418DT-1000Pa: Area Pane Left Bottom=0.48 m²; Area Pane Left Middle=0.38 m²; Area Pane Left Top=0.38 m²; Area Pane Right=2.49 m²; Clearvue Insulated LowE SHGC Value=0; Clearvue Insulated LowE U Value=7.9; Clearvue Insulated SHGC Value=0; Clearvue Insulated U Value=7.9; Clearvue SHGC Value=0; Clearvue U Value=7.9; Custom Sash Width=854 mm  [stored 2.80184 ft]; Custom Windload=1000 mm; Custom Window Height=1790 mm; Custom Window Width=2390 mm; DG Thickness Calc=5 mm  [stored 0.0164042 ft]; Depth Mullion=70 mm  [stored 0.229659 ft]; Energy Advantage SHGC Value=0; Energy Advantage U Value=7.9; Height=1790 mm; Height Panel 3=590 mm; Height Panel 4=1730 mm; Intruderprufe Insulated LowE SHGC Value=0.903; Intruderprufe Insulated LowE U Value=4.94; Intruderprufe Insulated SHGC Value=0.997; Intruderprufe Insulated U Value=5.99; Intruderprufe LowE SHGC Value=1.024; Intruderprufe LowE U Value=7.34; Intruderprufe SHGC Value=1.164; Intruderprufe U Value=10.33; Length Mullion=1790 mm; Length Transom=840 mm; Limit Sash Bottom Height Max=944 mm; Limit Sash Bottom Height Max Based On Top Sash=944 mm; Limit Sash Bottom Height Max Calc=944 mm; Limit Window Width Max=2430 mm; Limit Window Width Min=1130 mm; Max Pane Area=2.49 m²; Mullion Depth Windload Based=70 mm  [stored 0.229659 ft]; Offset Mullion Left=870 mm  [stored 2.85433 ft]; Offset Panel 4 Left=900 mm  [stored 2.95276 ft]; Width=2390 mm; Width Panel 1=840 mm; Width Panel 2=840 mm; Width Panel 3=840 mm; Width Panel 4=1460 mm; Width Sash 1=824 mm; Width Sash 2=824 mm; Width Sash Opening=854 mm  [stored 2.80184 ft]; Windload Design=1000 mm
- 38-2418DT-1500Pa: Area Pane Left Bottom=0.48 m²; Area Pane Left Middle=0.38 m²; Area Pane Left Top=0.38 m²; Area Pane Right=2.49 m²; Clearvue Insulated LowE SHGC Value=0; Clearvue Insulated LowE U Value=7.9; Clearvue Insulated SHGC Value=0; Clearvue Insulated U Value=7.9; Clearvue SHGC Value=0; Clearvue U Value=7.9; Custom Sash Width=854 mm  [stored 2.80184 ft]; Custom Windload=1500 mm; Custom Window Height=1790 mm; Custom Window Width=2390 mm; DG Thickness Calc=5 mm  [stored 0.0164042 ft]; Depth Mullion=70 mm  [stored 0.229659 ft]; Energy Advantage SHGC Value=0; Energy Advantage U Value=7.9; Height=1790 mm; Height Panel 3=590 mm; Height Panel 4=1730 mm; Intruderprufe Insulated LowE SHGC Value=0.903; Intruderprufe Insulated LowE U Value=4.94; Intruderprufe Insulated SHGC Value=0.997; Intruderprufe Insulated U Value=5.99; Intruderprufe LowE SHGC Value=1.024; Intruderprufe LowE U Value=7.34; Intruderprufe SHGC Value=1.164; Intruderprufe U Value=10.33; Length Mullion=1790 mm; Length Transom=840 mm; Limit Sash Bottom Height Max=944 mm; Limit Sash Bottom Height Max Based On Top Sash=944 mm; Limit Sash Bottom Height Max Calc=944 mm; Limit Window Width Max=2430 mm; Limit Window Width Min=1130 mm; Max Pane Area=2.49 m²; Mullion Depth Windload Based=70 mm  [stored 0.229659 ft]; Offset Mullion Left=870 mm  [stored 2.85433 ft]; Offset Panel 4 Left=900 mm  [stored 2.95276 ft]; Width=2390 mm; Width Panel 1=840 mm; Width Panel 2=840 mm; Width Panel 3=840 mm; Width Panel 4=1460 mm; Width Sash 1=824 mm; Width Sash 2=824 mm; Width Sash Opening=854 mm  [stored 2.80184 ft]; Windload Design=1500 mm
- 38-2418DT-2000Pa: Area Pane Left Bottom=0.48 m²; Area Pane Left Middle=0.38 m²; Area Pane Left Top=0.38 m²; Area Pane Right=2.49 m²; Clearvue Insulated LowE SHGC Value=0; Clearvue Insulated LowE U Value=7.9; Clearvue Insulated SHGC Value=0; Clearvue Insulated U Value=7.9; Clearvue SHGC Value=0; Clearvue U Value=7.9; Custom Sash Width=854 mm  [stored 2.80184 ft]; Custom Windload=2000 mm; Custom Window Height=1790 mm; Custom Window Width=2390 mm; DG Thickness Calc=5 mm  [stored 0.0164042 ft]; Depth Mullion=70 mm  [stored 0.229659 ft]; Energy Advantage SHGC Value=0; Energy Advantage U Value=7.9; Height=1790 mm; Height Panel 3=590 mm; Height Panel 4=1730 mm; Intruderprufe Insulated LowE SHGC Value=0.903; Intruderprufe Insulated LowE U Value=4.94; Intruderprufe Insulated SHGC Value=0.997; Intruderprufe Insulated U Value=5.99; Intruderprufe LowE SHGC Value=1.024; Intruderprufe LowE U Value=7.34; Intruderprufe SHGC Value=1.164; Intruderprufe U Value=10.33; Length Mullion=1790 mm; Length Transom=840 mm; Limit Sash Bottom Height Max=944 mm; Limit Sash Bottom Height Max Based On Top Sash=944 mm; Limit Sash Bottom Height Max Calc=944 mm; Limit Window Width Max=2430 mm; Limit Window Width Min=1130 mm; Max Pane Area=2.49 m²; Mullion Depth Windload Based=70 mm  [stored 0.229659 ft]; Offset Mullion Left=870 mm  [stored 2.85433 ft]; Offset Panel 4 Left=900 mm  [stored 2.95276 ft]; Width=2390 mm; Width Panel 1=840 mm; Width Panel 2=840 mm; Width Panel 3=840 mm; Width Panel 4=1460 mm; Width Sash 1=824 mm; Width Sash 2=824 mm; Width Sash Opening=854 mm  [stored 2.80184 ft]; Windload Design=2000 mm

note: [stored X ft] marks values corroborated as IEEE doubles in the binary element streams (Revit-internal decimal feet)

## geometry (parser evidence)
native form markers: Blend x4, Extrusion x1, Sweep x29
no freeform markers — native parametric forms only
